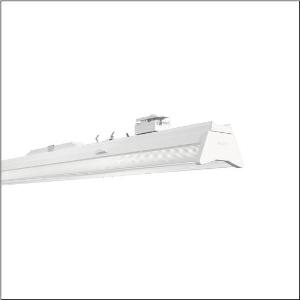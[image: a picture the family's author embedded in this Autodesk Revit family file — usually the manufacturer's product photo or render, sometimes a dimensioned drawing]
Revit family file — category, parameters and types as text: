
# Revit family: licross_11_performance_mo_51tm16mn4axg
name_source: partatom
category: Lighting Fixtures
units: mm (PartAtom-declared; Revit-internal decimal feet)

## family parameters
Cut with Voids When Loaded = No
Host = Face
Light Source = No
Part Type = Normal
Room Calculation Point = No
Round Connector Dimension = Use Diameter
Shared = No

## types (1)
- --- (1 x LED, 10160 lm, 55.3 W, 4000K)
    Apparent Load = 55 VA
    CIE Flux Codes = 66 88 96 79 100
    Color Rendering = 80
    Color Temperature = 4000K
    Default Elevation = 1800 mm
    Description = Licross 11 Performance MO, luminaire insert, of sheet steel, galvanised, coil coated, white, length: 1.500mm, width: 120mm, height: 123mm, LED rated luminous flux: 10.160lm, light colour: 840, SDCM (Standard Deviation of Colour Matching)MacAdam ≤ 2 SDCM (initial), control gear: ON/OFF Multilumen, with plug, 3-pole, with phase selection, mains connection: 220..240V, AC, 50/60Hz, rated input power: 55W, internal wiring halogen-free, primary light control with lens, of plastic, primary optical cover: cover, of PMMA, light emission: direct/indirect distribution, primary light characteristic: symmetric, protection rating (complete): IP40, insulation class (complete): insulation class I (protective earthing), certification: CE, ENEC, VDE, UKCA, protection symbol: D if used in an environment without relevant dust loads with corresponding accessories, impact resistance: IK06, permissible ambient temperature for indoor applications: -35..+40°C, corresponds to IFS (International Featured Standards) requirements for safety and quality in the food industry, reducing of maximum allowable ambient temperature of 5°C with ceiling mounting, LABS conformity tested according to VDMA 24364:2018-05, The light source and the operating device comply with the requirements of the Ecodesign Regulation (EU) 2019/2020 and are replaceable in accordance with this regulation, packaging unit: 1 piece
    Height = 114 mm
    Lamp = 1 x LED
    Lamp Light Flux = 10160 lm
    Lamp Power = 55.3 W
    Lamp count = 1
    Length = 1500 mm
    Luminous efficacy = 184 lm/W
    Manufacturer = Siteco
    ModVariant = No
    Model = 51TM16MN4AXG
    Mounting Place = Ceiling
    Mounting Type = Pendant
    Number of Poles = 1
    OnlyDefault = Yes
    Power Factor = 1
    Product Name = Licross 11 Performance MO
    Product group = luminaire insert | ceiling pendant
    ProductGroupID = 901
    Protection Class = Protection class I
    Protection Degree = IP 40
    RLX_Detail_Level = 1
    RLX_Emergency_Light_Flux = 0 lm
    RLX_Emergency_Type = 0
    RLX_Emergency_Type_DB = No
    RlxData = <blob elided: 32121 chars, md5=5565af6a>
    Socket = socket
    Standby Power = 0 W
    System Light Flux = 10160 lm
    System Power = 55 W
    Type Comments = factory setting: luminous flux: 100 % | (A | C | E) | 126 mA
    Type Image = l_1256138.jpg
    URL = http://relux.com
    VarID = @adj_092131
    Voltage = 0 V
    Weight = 0.00 kg
    Width = 120 mm

## geometry (parser evidence)
native form markers: Blend x4, Sweep x12
no freeform markers — native parametric forms only
